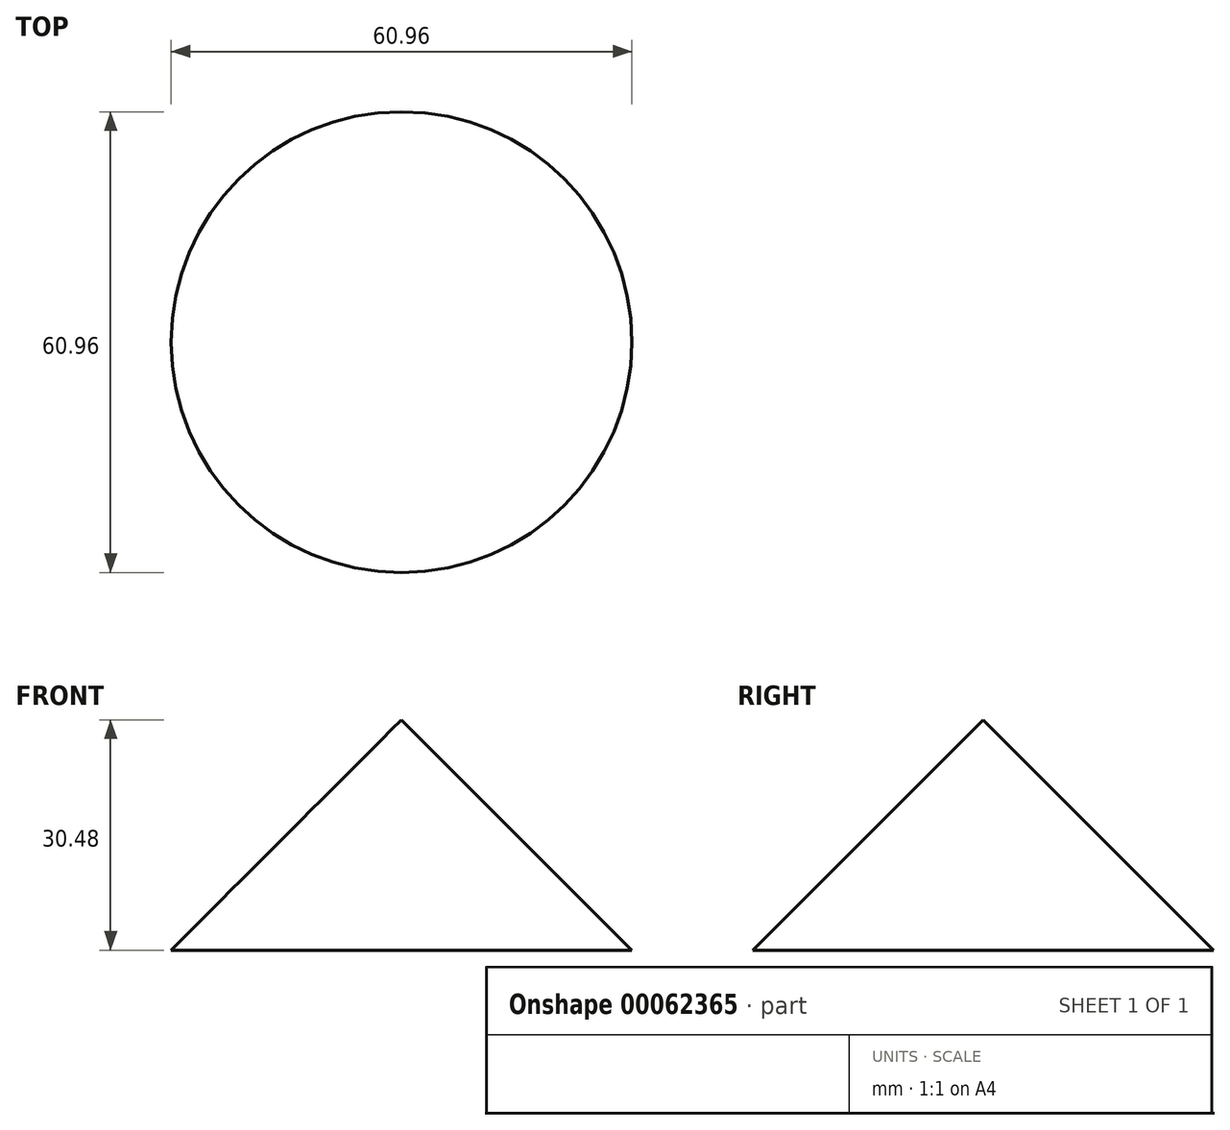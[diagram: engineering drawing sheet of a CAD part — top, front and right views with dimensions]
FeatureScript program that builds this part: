
annotation { "Feature Type Name" : "Feature", "Feature Type Description" : "" }
export const myFeature = defineFeature(function(context is Context, id is Id, definition is map)
    precondition{}
    {
        {
            var Q0;
            Q0=qCreatedBy(makeId("Front.planeOp"),FACE);
            var sketch = newSketch(context, id + "F0", { "sketchPlane" : qUnion([Q0])});
            skLineSegment(sketch, "E0", {"start": v(0, 0) * mm, "end": v(30.48, 0) * mm});
            skLineSegment(sketch, "E1", {"start": v(0, 0) * mm, "end": v(0, 30.48) * mm});
            skLineSegment(sketch, "E2", {"start": v(0, 30.48) * mm, "end": v(30.48, 0) * mm});
            skSolve(sketch);
        }
        {
            var Q0;
            Q0=makeQuery(id+"F0.imprint","IMPRINT",FACE,{"disambiguationData":[TD([[makeQuery(id+"F0.imprint","IMPRINT",EDGE,{"derivedFrom":sQuery(id+"F0.wireOp",EDGE,"E0")}),1.0]])]});
            var Q1;
            Q1=sQuery(id+"F0.wireOp",EDGE,"E1");
            revolve(context, id + "F1", {"entities" : qUnion([Q0]), "axis" : qUnion([Q1]), "revolveType" : RevolveType.FULL});
        }
        {
            var Q0;
            Q0=qCreatedBy(makeId("Top.planeOp"),FACE);
            var sketch = newSketch(context, id + "F2", { "sketchPlane" : qUnion([Q0])});
            skCircle(sketch, "E3", {"center": v(-47.42, -15.66) * mm, "radius": 15.24 * mm});
            skSolve(sketch);
        }
        {
            var Q0;
            Q0=makeQuery(id+"F2.imprint","IMPRINT",FACE,{"disambiguationData":[TD([[makeQuery(id+"F2.imprint","IMPRINT",EDGE,{"derivedFrom":sQuery(id+"F2.wireOp",EDGE,"E3")}),1.0]])]});
            extrude(context, id + "F3", {"entities" : qUnion([Q0]), "depth" : 30.48 * mm});
        }
        {
            var Q0;
            Q0=makeQuery(id+"F3.opExtrude","SWEPT_BODY",BODY,{"disambiguationData":[OSD([sQuery(id+"F2.wireOp",EDGE,"E3")])]});
            deleteBodies(context, id + "F4", {"entities" : qUnion([Q0])});
        }
    });
